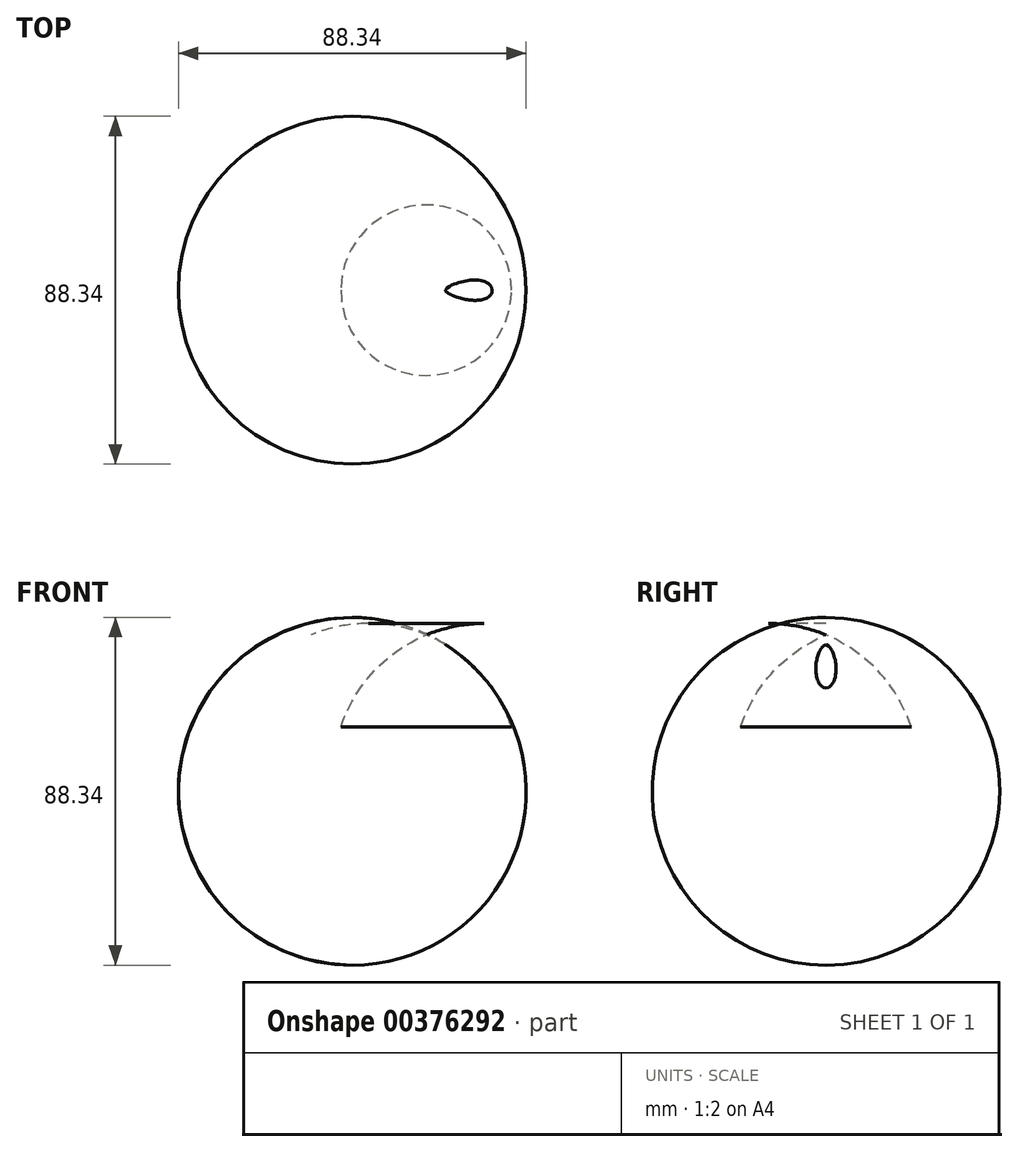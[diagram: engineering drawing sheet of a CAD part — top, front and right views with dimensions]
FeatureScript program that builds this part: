
annotation { "Feature Type Name" : "Feature", "Feature Type Description" : "" }
export const myFeature = defineFeature(function(context is Context, id is Id, definition is map)
    precondition{}
    {
        {
            var Q0;
            Q0=qCreatedBy(makeId("Front.planeOp"),FACE);
            var sketch = newSketch(context, id + "F0", { "sketchPlane" : qUnion([Q0])});
            skArc(sketch, "E0", {"start": v(0, 44.17) * mm, "mid": v(-44.17, 0) * mm, "end": v(0, -44.17) * mm});
            skLineSegment(sketch, "E1", {"start": v(0, 44.17) * mm, "end": v(0, -44.17) * mm});
            skSolve(sketch);
        }
        {
            var Q0;
            Q0 = qSketchRegion(id + "F0", true);
            var Q1;
            Q1=sQuery(id+"F0.wireOp",EDGE,"E1");
            revolve(context, id + "F1", {"entities" : qUnion([Q0]), "axis" : qUnion([Q1]), "revolveType" : RevolveType.FULL});
        }
        {
            var Q0;
            Q0=qCreatedBy(makeId("Front.planeOp"),FACE);
            var sketch = newSketch(context, id + "F2", { "sketchPlane" : qUnion([Q0])});
            skLineSegment(sketch, "E2", {"start": v(18.78, 39.74) * mm, "end": v(18.78, 16.33) * mm});
            skLineSegment(sketch, "E3", {"start": v(18.78, 16.33) * mm, "end": v(40.46, 16.33) * mm});
            skArc(sketch, "E4", {"start": v(40.46, 16.33) * mm, "mid": v(32.18, 30.4) * mm, "end": v(18.78, 39.74) * mm});
            skSolve(sketch);
        }
        {
            var Q0;
            Q0 = qSketchRegion(id + "F2", true);
            var Q1;
            Q1=sQuery(id+"F2.wireOp",EDGE,"E2");
            revolve(context, id + "F3", {"operationType" : NewBodyOperationType.REMOVE, "entities" : qUnion([Q0]), "axis" : qUnion([Q1]), "revolveType" : RevolveType.FULL, "oppositeDirection" : true});
        }
    });
